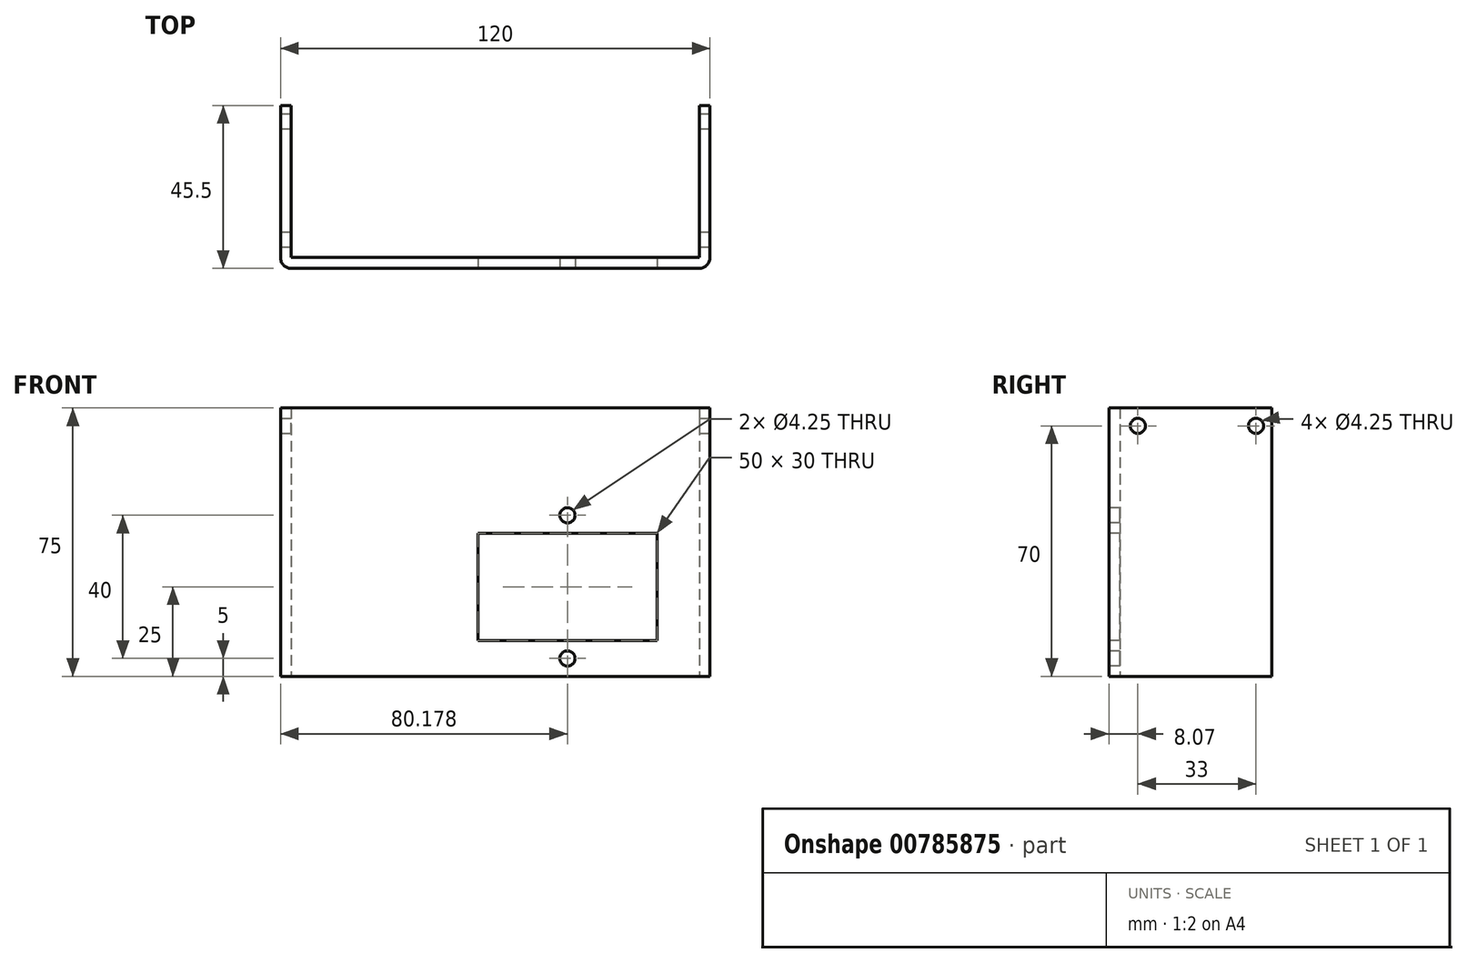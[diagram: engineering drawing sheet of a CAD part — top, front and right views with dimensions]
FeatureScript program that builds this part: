
annotation { "Feature Type Name" : "Feature", "Feature Type Description" : "" }
export const myFeature = defineFeature(function(context is Context, id is Id, definition is map)
    precondition{}
    {
        {
            var Q0;
            Q0=qCreatedBy(makeId("Top.planeOp"),FACE);
            var sketch = newSketch(context, id + "F0", { "sketchPlane" : qUnion([Q0])});
            skLineSegment(sketch, "E0", {"start": v(-28.58, 30.7) * mm, "end": v(-28.58, -11.8) * mm});
            skLineSegment(sketch, "E1", {"start": v(-28.58, -11.8) * mm, "end": v(85.42, -11.8) * mm});
            skLineSegment(sketch, "E2", {"start": v(85.42, -11.8) * mm, "end": v(85.42, 30.7) * mm});
            skLineSegment(sketch, "E3.0", {"start": v(-31.58, 30.7) * mm, "end": v(-31.58, -14.8) * mm});
            skLineSegment(sketch, "E4.0", {"start": v(-27.58, -14.8) * mm, "end": v(84.42, -14.8) * mm});
            skLineSegment(sketch, "E5.0", {"start": v(88.42, -14.8) * mm, "end": v(88.42, 30.7) * mm});
            skLineSegment(sketch, "E6", {"start": v(-28.58, 30.7) * mm, "end": v(-30.36, 30.7) * mm});
            skLineSegment(sketch, "E7", {"start": v(85.42, 30.7) * mm, "end": v(87.19, 30.7) * mm});
            skLineSegment(sketch, "E8", {"start": v(-30.36, 30.7) * mm, "end": v(-31.58, 30.7) * mm});
            skLineSegment(sketch, "E9", {"start": v(87.19, 30.7) * mm, "end": v(88.42, 30.7) * mm});
            skLineSegment(sketch, "E10", {"start": v(84.42, -14.8) * mm, "end": v(88.42, -14.8) * mm});
            skLineSegment(sketch, "E11", {"start": v(-27.58, -14.8) * mm, "end": v(-31.58, -14.8) * mm});
            skSolve(sketch);
        }
        {
            var Q0;
            Q0=makeQuery(id+"F0.imprint","IMPRINT",FACE,{"disambiguationData":[TD([[makeQuery(id+"F0.imprint","IMPRINT",EDGE,{"derivedFrom":sQuery(id+"F0.wireOp",EDGE,"E0")}),-1.0]])]});
            extrude(context, id + "F1", {"entities" : qUnion([Q0]), "depth" : 75 * mm, "offsetDistance" : 25 * mm});
        }
        {
            var Q0;
            Q0=makeQuery(id+"F1.opExtrude","SWEPT_FACE",FACE,{"disambiguationData":[OSD([sQuery(id+"F0.wireOp",EDGE,"E4.0")])]});
            var sketch = newSketch(context, id + "F2", { "sketchPlane" : qUnion([Q0])});
            skLineSegment(sketch, "E12.0", {"start": v(73.6, 40) * mm, "end": v(73.6, 10) * mm});
            skLineSegment(sketch, "E13.0", {"start": v(23.6, 40) * mm, "end": v(73.6, 40) * mm});
            skLineSegment(sketch, "E14.0", {"start": v(23.6, 40) * mm, "end": v(23.6, 10) * mm});
            skLineSegment(sketch, "E15.0", {"start": v(23.6, 10) * mm, "end": v(73.6, 10) * mm});
            skCircle(sketch, "E16", {"center": v(48.6, 45) * mm, "radius": 2.12 * mm});
            skCircle(sketch, "E17", {"center": v(48.6, 5) * mm, "radius": 2.12 * mm});
            skSolve(sketch);
        }
        {
            var Q0;
            Q0=makeQuery(id+"F2.imprint","IMPRINT",FACE,{"disambiguationData":[TD([[makeQuery(id+"F2.imprint","IMPRINT",EDGE,{"derivedFrom":sQuery(id+"F2.wireOp",EDGE,"E16")}),1.0]])]});
            var Q1;
            Q1=makeQuery(id+"F2.imprint","IMPRINT",FACE,{"disambiguationData":[TD([[makeQuery(id+"F2.imprint","IMPRINT",EDGE,{"derivedFrom":sQuery(id+"F2.wireOp",EDGE,"E17")}),1.0]])]});
            var Q2;
            Q2=makeQuery(id+"F2.imprint","IMPRINT",FACE,{"disambiguationData":[TD([[makeQuery(id+"F2.imprint","IMPRINT",EDGE,{"derivedFrom":sQuery(id+"F2.wireOp",EDGE,"E12.0")}),-1.0]])]});
            extrude(context, id + "F3", {"entities" : qUnion([Q0, Q1, Q2]), "operationType" : NewBodyOperationType.REMOVE, "oppositeDirection" : true, "depth" : 5 * mm, "offsetDistance" : 25 * mm});
        }
        {
            var Q0;
            Q0=makeQuery(id+"F1.opExtrude","SWEPT_FACE",FACE,{"disambiguationData":[OSD([sQuery(id+"F0.wireOp",EDGE,"E5.0")])]});
            var sketch = newSketch(context, id + "F4", { "sketchPlane" : qUnion([Q0])});
            skSolve(sketch);
        }
        {
            var Q0;
            {var subQ0=sQuery(id+"F0.wireOp",EDGE,"E5.0");Q0=makeQuery(id+"F4.imprint","IMPRINT",FACE,{"disambiguationData":[TD([[makeQuery(id+"F4.imprint","IMPRINT",EDGE,{"derivedFrom":makeQuery(id+"F1.opExtrude","CAP_EDGE",EDGE,{"disambiguationData":[OSD([subQ0])],"isStart":true})}),1.0]])]});}
            var sketch = newSketch(context, id + "F5", { "sketchPlane" : qUnion([Q0])});
            skCircle(sketch, "E18", {"center": v(-6.73, 70) * mm, "radius": 2.12 * mm});
            skCircle(sketch, "E19", {"center": v(26.27, 70) * mm, "radius": 2.12 * mm});
            skSolve(sketch);
        }
        {
            var Q0;
            Q0 = qSketchRegion(id + "F5", true);
            extrude(context, id + "F6", {"entities" : qUnion([Q0]), "operationType" : NewBodyOperationType.REMOVE, "oppositeDirection" : true, "depth" : 130 * mm, "offsetDistance" : 25 * mm});
        }
        {
            var Q0;
            Q0=makeQuery(id+"F1.opExtrude","SWEPT_EDGE",EDGE,{"disambiguationData":[OSD([sQuery(id+"F0.wireOp",EDGE,"E5.0"),sQuery(id+"F0.wireOp",EDGE,"E10")])]});
            var Q1;
            Q1=makeQuery(id+"F1.opExtrude","SWEPT_EDGE",EDGE,{"disambiguationData":[OSD([sQuery(id+"F0.wireOp",EDGE,"E3.0"),sQuery(id+"F0.wireOp",EDGE,"E11")])]});
            fillet(context, id + "F7", {"entities" : qUnion([Q0, Q1]), "radius" : 3 * mm, "tangentPropagation" : true, "allowEdgeOverflow" : false});
        }
    });
